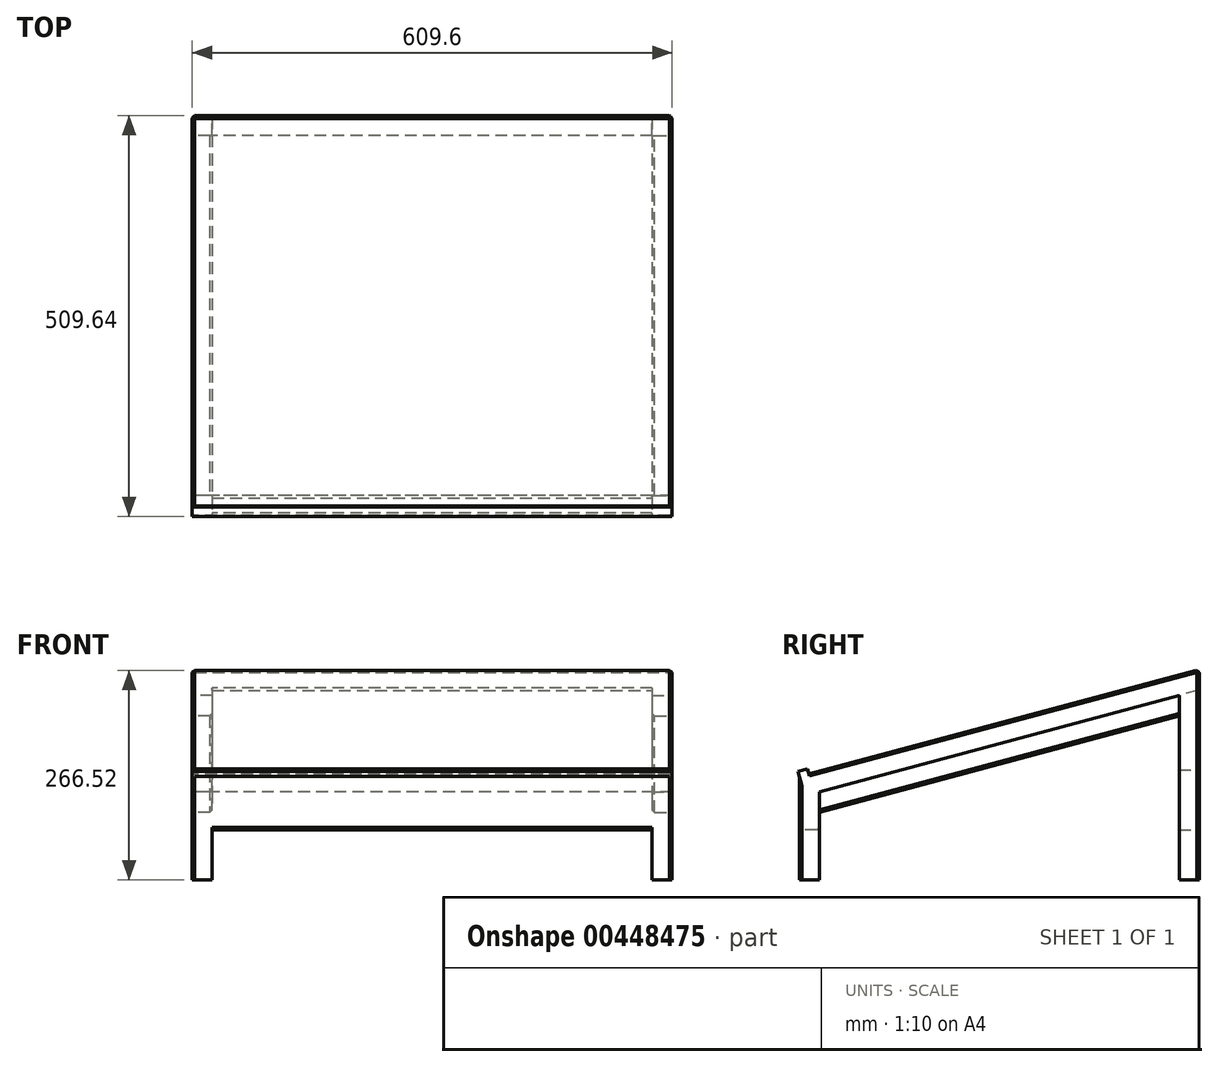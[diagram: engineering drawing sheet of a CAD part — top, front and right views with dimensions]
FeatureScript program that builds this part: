
annotation { "Feature Type Name" : "Feature", "Feature Type Description" : "" }
export const myFeature = defineFeature(function(context is Context, id is Id, definition is map)
    precondition{}
    {
        {
            var Q0;
            Q0=qCreatedBy(makeId("Right.planeOp"),FACE);
            var sketch = newSketch(context, id + "F0", { "sketchPlane" : qUnion([Q0])});
            skLineSegment(sketch, "E0", {"start": v(-243.02, 104.88) * mm, "end": v(252.7, 237.5) * mm});
            skLineSegment(sketch, "E1", {"start": v(-243.02, 104.88) * mm, "end": v(-244.67, 111.02) * mm});
            skLineSegment(sketch, "E2", {"start": v(-244.67, 111.02) * mm, "end": v(-256.93, 107.73) * mm});
            skLineSegment(sketch, "E3", {"start": v(-255.3, 101.6) * mm, "end": v(-256.93, 107.73) * mm});
            skPoint(sketch, "E4", {"position": v(252.7, 211.2) * mm});
            skLineSegment(sketch, "E5", {"start": v(252.7, 237.5) * mm, "end": v(252.7, 211.2) * mm});
            skLineSegment(sketch, "E6", {"start": v(252.7, 211.2) * mm, "end": v(-255.3, 75.3) * mm});
            skLineSegment(sketch, "E7", {"start": v(-255.3, 101.6) * mm, "end": v(-255.3, 75.3) * mm});
            skPoint(sketch, "E8.trimOffspring.end.orphan", {"position": v(252.7, 0) * mm});
            skSolve(sketch);
        }
        {
            var Q0;
            Q0 = qSketchRegion(id + "F0", true);
            extrude(context, id + "F1", {"entities" : qUnion([Q0]), "depth" : 609.6 * mm});
        }
        {
            var Q0;
            Q0=makeQuery(id+"F1.opExtrude","SWEPT_FACE",FACE,{"disambiguationData":[OSD([sQuery(id+"F0.wireOp",EDGE,"E5")])]});
            var sketch = newSketch(context, id + "F2", { "sketchPlane" : qUnion([Q0])});
            skLineSegment(sketch, "E9.top", {"start": v(-609.6, -30.1) * mm, "end": v(-584.2, -30.1) * mm});
            skLineSegment(sketch, "E9.left", {"start": v(-609.6, 211.2) * mm, "end": v(-609.6, -30.1) * mm});
            skLineSegment(sketch, "E9.right", {"start": v(-584.2, 211.2) * mm, "end": v(-584.2, 109.6) * mm});
            skLineSegment(sketch, "E10.top", {"start": v(0, -30.1) * mm, "end": v(-25.4, -30.1) * mm});
            skLineSegment(sketch, "E10.left", {"start": v(0, 211.2) * mm, "end": v(0, -30.1) * mm});
            skLineSegment(sketch, "E10.right", {"start": v(-25.4, 211.2) * mm, "end": v(-25.4, 109.6) * mm});
            skLineSegment(sketch, "E11", {"start": v(-609.6, 211.2) * mm, "end": v(-584.2, 211.2) * mm});
            skLineSegment(sketch, "E12", {"start": v(0, 211.2) * mm, "end": v(-25.4, 211.2) * mm});
            skLineSegment(sketch, "E13.bottom", {"start": v(-584.2, 109.6) * mm, "end": v(-25.4, 109.6) * mm});
            skLineSegment(sketch, "E13.top", {"start": v(-584.2, 33.4) * mm, "end": v(-25.4, 33.4) * mm});
            skLineSegment(sketch, "E14.trimOffspring", {"start": v(-584.2, 33.4) * mm, "end": v(-584.2, -30.1) * mm});
            skLineSegment(sketch, "E15.trimOffspring", {"start": v(-25.4, 33.4) * mm, "end": v(-25.4, -30.1) * mm});
            skSolve(sketch);
        }
        {
            var Q0;
            Q0 = qSketchRegion(id + "F2", true);
            extrude(context, id + "F3", {"entities" : qUnion([Q0]), "operationType" : NewBodyOperationType.ADD, "oppositeDirection" : true, "depth" : 25.4 * mm});
        }
        {
            var Q0;
            Q0=makeQuery(id+"F1.opExtrude","SWEPT_FACE",FACE,{"disambiguationData":[OSD([sQuery(id+"F0.wireOp",EDGE,"E7")])]});
            var sketch = newSketch(context, id + "F4", { "sketchPlane" : qUnion([Q0])});
            skLineSegment(sketch, "E16.bottom", {"start": v(0, 101.6) * mm, "end": v(25.4, 101.6) * mm});
            skLineSegment(sketch, "E16.top", {"start": v(0, -30.1) * mm, "end": v(25.4, -30.1) * mm});
            skLineSegment(sketch, "E16.left", {"start": v(0, 101.6) * mm, "end": v(0, -30.1) * mm});
            skLineSegment(sketch, "E16.right", {"start": v(25.4, 101.6) * mm, "end": v(25.4, 84.2) * mm});
            skLineSegment(sketch, "E17.bottom", {"start": v(609.6, 101.6) * mm, "end": v(584.2, 101.6) * mm});
            skLineSegment(sketch, "E17.top", {"start": v(609.6, -30.1) * mm, "end": v(584.2, -30.1) * mm});
            skLineSegment(sketch, "E17.left", {"start": v(609.6, 101.6) * mm, "end": v(609.6, -30.1) * mm});
            skLineSegment(sketch, "E17.right", {"start": v(584.2, 101.6) * mm, "end": v(584.2, 84.2) * mm});
            skLineSegment(sketch, "E18.bottom", {"start": v(25.4, 84.2) * mm, "end": v(584.2, 84.2) * mm});
            skLineSegment(sketch, "E18.top", {"start": v(25.4, 33.4) * mm, "end": v(584.2, 33.4) * mm});
            skLineSegment(sketch, "E19.trimOffspring", {"start": v(25.4, 33.4) * mm, "end": v(25.4, -30.1) * mm});
            skLineSegment(sketch, "E20.trimOffspring", {"start": v(584.2, 33.4) * mm, "end": v(584.2, -30.1) * mm});
            skSolve(sketch);
        }
        {
            var Q0;
            Q0 = qSketchRegion(id + "F4", true);
            extrude(context, id + "F5", {"entities" : qUnion([Q0]), "operationType" : NewBodyOperationType.ADD, "oppositeDirection" : true, "depth" : 25.4 * mm});
        }
        {
            var Q0;
            Q0=makeQuery(id+"F5.boolean.opBoolean","MERGE",FACE,{"derivedFrom":[makeQuery(id+"F3.boolean.opBoolean","MERGE",FACE,{"derivedFrom":[makeQuery(id+"F1.opExtrude","CAP_FACE",FACE,{"disambiguationData":[OSD([sQuery(id+"F0.wireOp",EDGE,"E0"),sQuery(id+"F0.wireOp",EDGE,"E1"),sQuery(id+"F0.wireOp",EDGE,"E2"),sQuery(id+"F0.wireOp",EDGE,"E3"),sQuery(id+"F0.wireOp",EDGE,"E5"),sQuery(id+"F0.wireOp",EDGE,"E6"),sQuery(id+"F0.wireOp",EDGE,"E7")])],"isStart":true}),makeQuery(id+"F3.opExtrude","SWEPT_FACE",FACE,{"disambiguationData":[OSD([sQuery(id+"F2.wireOp",EDGE,"E10.left")])]})]}),makeQuery(id+"F5.opExtrude","SWEPT_FACE",FACE,{"disambiguationData":[OSD([sQuery(id+"F4.wireOp",EDGE,"E16.left")])]})]});
            var sketch = newSketch(context, id + "F6", { "sketchPlane" : qUnion([Q0])});
            skLineSegment(sketch, "E21", {"start": v(-227.3, 204.4) * mm, "end": v(229.9, 82.1) * mm});
            skLineSegment(sketch, "E22", {"start": v(229.9, 82.1) * mm, "end": v(229.9, 55.8) * mm});
            skLineSegment(sketch, "E23", {"start": v(229.9, 55.8) * mm, "end": v(-227.3, 178.1) * mm});
            skLineSegment(sketch, "E24", {"start": v(-227.3, 178.1) * mm, "end": v(-227.3, 204.4) * mm});
            skSolve(sketch);
        }
        {
            var Q0;
            Q0 = qSketchRegion(id + "F6", true);
            extrude(context, id + "F7", {"entities" : qUnion([Q0]), "oppositeDirection" : true, "depth" : 25.4 * mm});
        }
        {
            var Q0;
            Q0=makeQuery(id+"F5.boolean.opBoolean","MERGE",FACE,{"derivedFrom":[makeQuery(id+"F3.boolean.opBoolean","MERGE",FACE,{"derivedFrom":[makeQuery(id+"F1.opExtrude","CAP_FACE",FACE,{"disambiguationData":[OSD([sQuery(id+"F0.wireOp",EDGE,"E0"),sQuery(id+"F0.wireOp",EDGE,"E1"),sQuery(id+"F0.wireOp",EDGE,"E2"),sQuery(id+"F0.wireOp",EDGE,"E3"),sQuery(id+"F0.wireOp",EDGE,"E5"),sQuery(id+"F0.wireOp",EDGE,"E6"),sQuery(id+"F0.wireOp",EDGE,"E7")])],"isStart":false}),makeQuery(id+"F3.opExtrude","SWEPT_FACE",FACE,{"disambiguationData":[OSD([sQuery(id+"F2.wireOp",EDGE,"E9.left")])]})]}),makeQuery(id+"F5.opExtrude","SWEPT_FACE",FACE,{"disambiguationData":[OSD([sQuery(id+"F4.wireOp",EDGE,"E17.left")])]})]});
            var sketch = newSketch(context, id + "F8", { "sketchPlane" : qUnion([Q0])});
            skLineSegment(sketch, "E25", {"start": v(-229.9, 82.1) * mm, "end": v(227.3, 204.4) * mm});
            skLineSegment(sketch, "E26", {"start": v(227.3, 204.4) * mm, "end": v(227.3, 178.1) * mm});
            skLineSegment(sketch, "E27", {"start": v(227.3, 178.1) * mm, "end": v(-229.9, 55.8) * mm});
            skLineSegment(sketch, "E28", {"start": v(-229.9, 55.8) * mm, "end": v(-229.9, 82.1) * mm});
            skSolve(sketch);
        }
        {
            var Q0;
            Q0 = qSketchRegion(id + "F8", true);
            extrude(context, id + "F9", {"entities" : qUnion([Q0]), "oppositeDirection" : true, "depth" : 25.4 * mm});
        }
        {
            var Q0;
            Q0=makeQuery(id+"F1.opExtrude","CAP_EDGE",EDGE,{"disambiguationData":[OSD([sQuery(id+"F0.wireOp",EDGE,"E0")])],"isStart":true});
            var Q1;
            Q1=makeQuery(id+"F1.opExtrude","SWEPT_EDGE",EDGE,{"disambiguationData":[OSD([sQuery(id+"F0.wireOp",EDGE,"E0"),sQuery(id+"F0.wireOp",EDGE,"E5")])]});
            var Q2;
            Q2=makeQuery(id+"F1.opExtrude","CAP_EDGE",EDGE,{"disambiguationData":[OSD([sQuery(id+"F0.wireOp",EDGE,"E0")])],"isStart":false});
            chamfer(context, id + "F10", {"entities" : qUnion([Q0, Q1, Q2]), "width" : 3.17 * mm, "tangentPropagation" : true});
        }
        {
            var Q0;
            Q0=makeQuery(id+"F9.opExtrude","CAP_EDGE",EDGE,{"disambiguationData":[OSD([sQuery(id+"F8.wireOp",EDGE,"E27")])],"isStart":true});
            var Q1;
            Q1=makeQuery(id+"F9.opExtrude","CAP_EDGE",EDGE,{"disambiguationData":[OSD([sQuery(id+"F8.wireOp",EDGE,"E27")])],"isStart":false});
            var Q2;
            Q2=makeQuery(id+"F7.opExtrude","CAP_EDGE",EDGE,{"disambiguationData":[OSD([sQuery(id+"F6.wireOp",EDGE,"E23")])],"isStart":false});
            var Q3;
            Q3=makeQuery(id+"F7.opExtrude","CAP_EDGE",EDGE,{"disambiguationData":[OSD([sQuery(id+"F6.wireOp",EDGE,"E23")])],"isStart":true});
            var Q4;
            Q4=makeQuery(id+"F5.boolean.opBoolean","MERGE",EDGE,{"derivedFrom":[makeQuery(id+"F1.opExtrude","CAP_EDGE",EDGE,{"disambiguationData":[OSD([sQuery(id+"F0.wireOp",EDGE,"E7")])],"isStart":false}),makeQuery(id+"F5.opExtrude","CAP_EDGE",EDGE,{"disambiguationData":[OSD([sQuery(id+"F4.wireOp",EDGE,"E17.left")])],"isStart":true})]});
            var Q5;
            Q5=makeQuery(id+"F3.boolean.opBoolean","MERGE",EDGE,{"derivedFrom":[makeQuery(id+"F1.opExtrude","CAP_EDGE",EDGE,{"disambiguationData":[OSD([sQuery(id+"F0.wireOp",EDGE,"E5")])],"isStart":false}),makeQuery(id+"F3.opExtrude","CAP_EDGE",EDGE,{"disambiguationData":[OSD([sQuery(id+"F2.wireOp",EDGE,"E9.left")])],"isStart":true})]});
            var Q6;
            Q6=makeQuery(id+"F5.boolean.opBoolean","MERGE",EDGE,{"derivedFrom":[makeQuery(id+"F1.opExtrude","CAP_EDGE",EDGE,{"disambiguationData":[OSD([sQuery(id+"F0.wireOp",EDGE,"E7")])],"isStart":true}),makeQuery(id+"F5.opExtrude","CAP_EDGE",EDGE,{"disambiguationData":[OSD([sQuery(id+"F4.wireOp",EDGE,"E16.left")])],"isStart":true})]});
            chamfer(context, id + "F11", {"entities" : qUnion([Q0, Q1, Q2, Q3, Q4, Q5, Q6]), "width" : 3.17 * mm, "tangentPropagation" : true});
        }
        {
            var Q0;
            Q0=makeQuery(id+"F3.boolean.opBoolean","MERGE",EDGE,{"derivedFrom":[makeQuery(id+"F1.opExtrude","CAP_EDGE",EDGE,{"disambiguationData":[OSD([sQuery(id+"F0.wireOp",EDGE,"E5")])],"isStart":true}),makeQuery(id+"F3.opExtrude","CAP_EDGE",EDGE,{"disambiguationData":[OSD([sQuery(id+"F2.wireOp",EDGE,"E10.left")])],"isStart":true})]});
            var Q1;
            {var subQ0=sQuery(id+"F2.wireOp",EDGE,"E9.left");var subQ1=sQuery(id+"F0.wireOp",EDGE,"E5");Q1=makeQuery(id+"F11.opChamfer","BLEND_EDGE",EDGE,{"blendedFrom":[makeQuery(id+"F3.boolean.opBoolean","MERGE",EDGE,{"derivedFrom":[makeQuery(id+"F1.opExtrude","CAP_EDGE",EDGE,{"disambiguationData":[OSD([subQ1])],"isStart":false}),makeQuery(id+"F3.opExtrude","CAP_EDGE",EDGE,{"disambiguationData":[OSD([subQ0])],"isStart":true})]}),makeQuery(id+"F3.boolean.opBoolean","MERGE",FACE,{"derivedFrom":[makeQuery(id+"F1.opExtrude","SWEPT_FACE",FACE,{"disambiguationData":[OSD([subQ1])]}),makeQuery(id+"F3.opExtrude","CAP_FACE",FACE,{"disambiguationData":[OSD([sQuery(id+"F2.wireOp",EDGE,"E9.top"),subQ0,sQuery(id+"F2.wireOp",EDGE,"E9.right"),sQuery(id+"F2.wireOp",EDGE,"E10.top"),sQuery(id+"F2.wireOp",EDGE,"E10.left"),sQuery(id+"F2.wireOp",EDGE,"E10.right"),sQuery(id+"F2.wireOp",EDGE,"E11"),sQuery(id+"F2.wireOp",EDGE,"E12"),sQuery(id+"F2.wireOp",EDGE,"E13.bottom"),sQuery(id+"F2.wireOp",EDGE,"E13.top"),sQuery(id+"F2.wireOp",EDGE,"E14.trimOffspring"),sQuery(id+"F2.wireOp",EDGE,"E15.trimOffspring")])],"isStart":true})]})],"blendedInto":[makeQuery(id+"F3.boolean.opBoolean","MERGE",FACE,{"derivedFrom":[makeQuery(id+"F1.opExtrude","SWEPT_FACE",FACE,{"disambiguationData":[OSD([subQ1])]}),makeQuery(id+"F3.opExtrude","CAP_FACE",FACE,{"disambiguationData":[OSD([sQuery(id+"F2.wireOp",EDGE,"E9.top"),subQ0,sQuery(id+"F2.wireOp",EDGE,"E9.right"),sQuery(id+"F2.wireOp",EDGE,"E10.top"),sQuery(id+"F2.wireOp",EDGE,"E10.left"),sQuery(id+"F2.wireOp",EDGE,"E10.right"),sQuery(id+"F2.wireOp",EDGE,"E11"),sQuery(id+"F2.wireOp",EDGE,"E12"),sQuery(id+"F2.wireOp",EDGE,"E13.bottom"),sQuery(id+"F2.wireOp",EDGE,"E13.top"),sQuery(id+"F2.wireOp",EDGE,"E14.trimOffspring"),sQuery(id+"F2.wireOp",EDGE,"E15.trimOffspring")])],"isStart":true})]})]});}
            chamfer(context, id + "F12", {"entities" : qUnion([Q0, Q1]), "width" : 3.17 * mm, "tangentPropagation" : true});
        }
        {
            var Q0;
            Q0=makeQuery(id+"F1.opExtrude","SWEPT_EDGE",EDGE,{"disambiguationData":[OSD([sQuery(id+"F0.wireOp",EDGE,"E5"),sQuery(id+"F0.wireOp",EDGE,"E6")])]});
            chamfer(context, id + "F13", {"entities" : qUnion([Q0]), "width" : 3.17 * mm, "tangentPropagation" : true});
        }
        {
            var Q0;
            Q0=makeQuery(id+"F5.opExtrude","CAP_EDGE",EDGE,{"disambiguationData":[OSD([sQuery(id+"F4.wireOp",EDGE,"E18.top")])],"isStart":true});
            var Q1;
            Q1=makeQuery(id+"F5.opExtrude","CAP_EDGE",EDGE,{"disambiguationData":[OSD([sQuery(id+"F4.wireOp",EDGE,"E18.top")])],"isStart":false});
            chamfer(context, id + "F14", {"entities" : qUnion([Q0, Q1]), "width" : 3.17 * mm, "tangentPropagation" : true});
        }
    });
